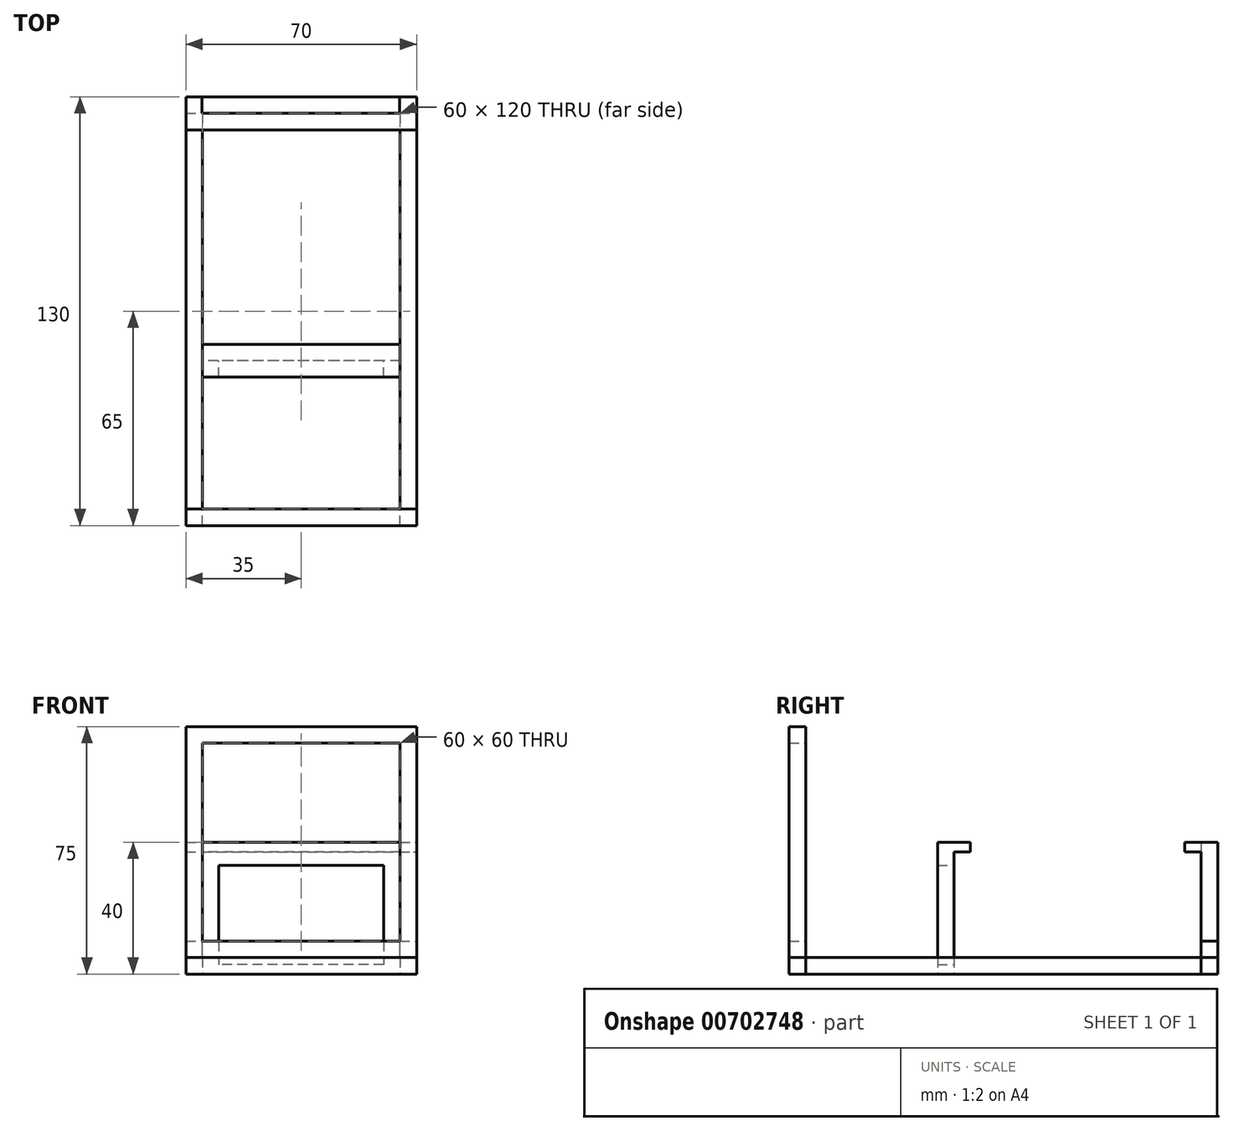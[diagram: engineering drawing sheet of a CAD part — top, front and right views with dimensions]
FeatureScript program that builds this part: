
annotation { "Feature Type Name" : "Feature", "Feature Type Description" : "" }
export const myFeature = defineFeature(function(context is Context, id is Id, definition is map)
    precondition{}
    {
        {
            var Q0;
            Q0=qCreatedBy(makeId("Top.planeOp"),FACE);
            var sketch = newSketch(context, id + "F0", { "sketchPlane" : qUnion([Q0])});
            skLineSegment(sketch, "E0.bottom", {"start": v(-35, 65) * mm, "end": v(35, 65) * mm});
            skLineSegment(sketch, "E0.top", {"start": v(-35, -65) * mm, "end": v(35, -65) * mm});
            skLineSegment(sketch, "E0.left", {"start": v(-35, 65) * mm, "end": v(-35, -65) * mm});
            skLineSegment(sketch, "E0.right", {"start": v(35, 65) * mm, "end": v(35, -65) * mm});
            skPoint(sketch, "E0.middle", {"position": v(0, 0) * mm});
            skLineSegment(sketch, "E1.bottom", {"start": v(-30, 60) * mm, "end": v(30, 60) * mm});
            skLineSegment(sketch, "E1.top", {"start": v(-30, -60) * mm, "end": v(30, -60) * mm});
            skLineSegment(sketch, "E1.left", {"start": v(-30, 60) * mm, "end": v(-30, -60) * mm});
            skLineSegment(sketch, "E1.right", {"start": v(30, 60) * mm, "end": v(30, -60) * mm});
            skLineSegment(sketch, "E2.bottom", {"start": v(-30, 60) * mm, "end": v(30, 60) * mm, "construction": true});
            skLineSegment(sketch, "E2.top", {"start": v(-30, -15) * mm, "end": v(30, -15) * mm, "construction": true});
            skLineSegment(sketch, "E2.left", {"start": v(-30, 60) * mm, "end": v(-30, -15) * mm, "construction": true});
            skLineSegment(sketch, "E2.right", {"start": v(30, 60) * mm, "end": v(30, -15) * mm, "construction": true});
            skLineSegment(sketch, "E3.bottom", {"start": v(-30, -15) * mm, "end": v(30, -15) * mm});
            skLineSegment(sketch, "E3.top", {"start": v(-30, -20) * mm, "end": v(30, -20) * mm});
            skLineSegment(sketch, "E3.left", {"start": v(-30, -15) * mm, "end": v(-30, -20) * mm});
            skLineSegment(sketch, "E3.right", {"start": v(30, -15) * mm, "end": v(30, -20) * mm});
            skLineSegment(sketch, "E4.top", {"start": v(-35, -60) * mm, "end": v(35, -60) * mm});
            skLineSegment(sketch, "E4.left", {"start": v(-35, -65) * mm, "end": v(-35, -60) * mm});
            skLineSegment(sketch, "E4.right", {"start": v(35, -65) * mm, "end": v(35, -60) * mm});
            skPoint(sketch, "E5.oppositeSnap0", {"position": v(0, 60) * mm});
            skLineSegment(sketch, "E5.top", {"start": v(-35, 60) * mm, "end": v(35, 60) * mm});
            skLineSegment(sketch, "E5.left", {"start": v(-35, 65) * mm, "end": v(-35, 60) * mm});
            skLineSegment(sketch, "E5.right", {"start": v(35, 65) * mm, "end": v(35, 60) * mm});
            skSolve(sketch);
        }
        {
            var Q0;
            Q0=makeQuery(id+"F0.imprint","IMPRINT",FACE,{"disambiguationData":[TD([[makeQuery(id+"F0.imprint","IMPRINT",EDGE,{"derivedFrom":sQuery(id+"F0.wireOp",EDGE,"E0.bottom")}),-1.0]])]});
            var Q1;
            Q1=makeQuery(id+"F0.imprint","IMPRINT",FACE,{"disambiguationData":[TD([[makeQuery(id+"F0.imprint","IMPRINT",EDGE,{"derivedFrom":sQuery(id+"F0.wireOp",EDGE,"E3.bottom")}),-1.0]])]});
            extrude(context, id + "F1", {"entities" : qUnion([Q0, Q1]), "depth" : 10 * mm, "offsetDistance" : 25 * mm});
        }
        {
            var Q0;
            Q0=makeQuery(id+"F0.imprint","IMPRINT",FACE,{"disambiguationData":[TD([[makeQuery(id+"F0.imprint","IMPRINT",EDGE,{"derivedFrom":sQuery(id+"F0.wireOp",EDGE,"E0.top")}),1.0]])]});
            extrude(context, id + "F2", {"entities" : qUnion([Q0]), "operationType" : NewBodyOperationType.ADD, "depth" : 75 * mm, "offsetDistance" : 25 * mm});
        }
        {
            var Q0;
            Q0=makeQuery(id+"F2.opExtrude","SWEPT_FACE",FACE,{"disambiguationData":[OSD([sQuery(id+"F0.wireOp",EDGE,"E4.top")])]});
            var sketch = newSketch(context, id + "F3", { "sketchPlane" : qUnion([Q0])});
            skLineSegment(sketch, "E6.bottom", {"start": v(-30, 10) * mm, "end": v(30, 10) * mm});
            skLineSegment(sketch, "E6.top", {"start": v(-30, 70) * mm, "end": v(30, 70) * mm});
            skLineSegment(sketch, "E6.left", {"start": v(-30, 10) * mm, "end": v(-30, 70) * mm});
            skLineSegment(sketch, "E6.right", {"start": v(30, 10) * mm, "end": v(30, 70) * mm});
            skSolve(sketch);
        }
        {
            var Q0;
            Q0=makeQuery(id+"F0.imprint","IMPRINT",FACE,{"disambiguationData":[TD([[makeQuery(id+"F0.imprint","IMPRINT",EDGE,{"derivedFrom":sQuery(id+"F0.wireOp",EDGE,"E3.bottom")}),-1.0]])]});
            extrude(context, id + "F4", {"entities" : qUnion([Q0]), "operationType" : NewBodyOperationType.ADD, "depth" : 40 * mm, "offsetDistance" : 25 * mm});
        }
        {
            var Q0;
            Q0=makeQuery(id+"F0.imprint","IMPRINT",FACE,{"disambiguationData":[TD([[makeQuery(id+"F0.imprint","IMPRINT",EDGE,{"derivedFrom":sQuery(id+"F0.wireOp",EDGE,"E0.bottom")}),-1.0]])]});
            extrude(context, id + "F5", {"entities" : qUnion([Q0]), "depth" : 40 * mm, "offsetDistance" : 25 * mm});
        }
        {
            var Q0;
            {var subQ6=sQuery(id+"F0.wireOp",EDGE,"E0.left");Q0=makeQuery(id+"F0.imprint","IMPRINT",FACE,{"disambiguationData":[TD([[makeQuery(id+"F0.imprint","IMPRINT",EDGE,{"derivedFrom":subQ6}),1.0]])]});}
            var Q1;
            {var subQ6=sQuery(id+"F0.wireOp",EDGE,"E0.right");Q1=makeQuery(id+"F0.imprint","IMPRINT",FACE,{"disambiguationData":[TD([[makeQuery(id+"F0.imprint","IMPRINT",EDGE,{"derivedFrom":subQ6}),-1.0]])]});}
            extrude(context, id + "F6", {"entities" : qUnion([Q0, Q1]), "depth" : 5 * mm, "offsetDistance" : 25 * mm});
        }
        {
            var Q0;
            {var subQ0=sQuery(id+"F0.wireOp",EDGE,"E3.bottom");Q0=makeQuery(id+"F4.boolean.opBoolean","MERGE",FACE,{"derivedFrom":[makeQuery(id+"F1.opExtrude","SWEPT_FACE",FACE,{"disambiguationData":[OSD([subQ0])]}),makeQuery(id+"F4.opExtrude","SWEPT_FACE",FACE,{"disambiguationData":[OSD([subQ0])]})]});}
            var sketch = newSketch(context, id + "F7", { "sketchPlane" : qUnion([Q0])});
            skLineSegment(sketch, "E7.bottom", {"start": v(-30, 40) * mm, "end": v(30, 40) * mm});
            skLineSegment(sketch, "E7.top", {"start": v(-30, 37) * mm, "end": v(30, 37) * mm});
            skLineSegment(sketch, "E7.left", {"start": v(-30, 40) * mm, "end": v(-30, 37) * mm});
            skLineSegment(sketch, "E7.right", {"start": v(30, 40) * mm, "end": v(30, 37) * mm});
            skLineSegment(sketch, "E8.bottom", {"start": v(-25, 32.92) * mm, "end": v(25, 32.92) * mm});
            skLineSegment(sketch, "E8.top", {"start": v(-25, 2.92) * mm, "end": v(25, 2.92) * mm});
            skLineSegment(sketch, "E8.left", {"start": v(-25, 32.92) * mm, "end": v(-25, 2.92) * mm});
            skLineSegment(sketch, "E8.right", {"start": v(25, 32.92) * mm, "end": v(25, 2.92) * mm});
            skPoint(sketch, "E8.middle", {"position": v(0, 17.92) * mm});
            skSolve(sketch);
        }
        {
            var Q0;
            Q0=makeQuery(id+"F5.opExtrude","SWEPT_FACE",FACE,{"disambiguationData":[OSD([sQuery(id+"F0.wireOp",EDGE,"E5.top")])]});
            var sketch = newSketch(context, id + "F8", { "sketchPlane" : qUnion([Q0])});
            skLineSegment(sketch, "E9.bottom", {"start": v(-35, 40) * mm, "end": v(35, 40) * mm});
            skLineSegment(sketch, "E9.top", {"start": v(-35, 37) * mm, "end": v(35, 37) * mm});
            skLineSegment(sketch, "E9.left", {"start": v(-35, 40) * mm, "end": v(-35, 37) * mm});
            skLineSegment(sketch, "E9.right", {"start": v(35, 40) * mm, "end": v(35, 37) * mm});
            skSolve(sketch);
        }
        {
            var Q0;
            Q0 = qSketchRegion(id + "F8", true);
            extrude(context, id + "F9", {"entities" : qUnion([Q0]), "operationType" : NewBodyOperationType.ADD, "depth" : 5 * mm, "offsetDistance" : 25 * mm});
        }
        {
            var Q0;
            Q0 = qSketchRegion(id + "F3", true);
            extrude(context, id + "F10", {"entities" : qUnion([Q0]), "operationType" : NewBodyOperationType.REMOVE, "oppositeDirection" : true, "depth" : 25 * mm, "offsetDistance" : 25 * mm});
        }
        {
            var Q0;
            Q0=makeQuery(id+"F7.imprint","IMPRINT",FACE,{"disambiguationData":[TD([[makeQuery(id+"F7.imprint","IMPRINT",EDGE,{"derivedFrom":sQuery(id+"F7.wireOp",EDGE,"E7.bottom")}),1.0]])]});
            extrude(context, id + "F11", {"entities" : qUnion([Q0]), "operationType" : NewBodyOperationType.ADD, "depth" : 5 * mm, "offsetDistance" : 25 * mm});
        }
        {
            var Q0;
            Q0=makeQuery(id+"F7.imprint","IMPRINT",FACE,{"disambiguationData":[TD([[makeQuery(id+"F7.imprint","IMPRINT",EDGE,{"derivedFrom":sQuery(id+"F7.wireOp",EDGE,"E8.bottom")}),-1.0]])]});
            extrude(context, id + "F12", {"entities" : qUnion([Q0]), "operationType" : NewBodyOperationType.REMOVE, "oppositeDirection" : true, "depth" : 5 * mm, "offsetDistance" : 25 * mm});
        }
        {
            var Q0;
            Q0=makeQuery(id+"F5.opExtrude","SWEPT_FACE",FACE,{"disambiguationData":[OSD([sQuery(id+"F0.wireOp",EDGE,"E0.bottom")])]});
            var sketch = newSketch(context, id + "F13", { "sketchPlane" : qUnion([Q0])});
            skLineSegment(sketch, "E10.bottom", {"start": v(-29.89, 40) * mm, "end": v(30.11, 40) * mm});
            skLineSegment(sketch, "E10.top", {"start": v(-29.89, 5) * mm, "end": v(30.11, 5) * mm});
            skLineSegment(sketch, "E10.left", {"start": v(-29.89, 40) * mm, "end": v(-29.89, 5) * mm});
            skLineSegment(sketch, "E10.right", {"start": v(30.11, 40) * mm, "end": v(30.11, 5) * mm});
            skSolve(sketch);
        }
        {
            var Q0;
            Q0=makeQuery(id+"F13.imprint","IMPRINT",FACE,{"disambiguationData":[TD([[makeQuery(id+"F13.imprint","IMPRINT",EDGE,{"derivedFrom":sQuery(id+"F13.wireOp",EDGE,"E10.bottom")}),1.0]])]});
            extrude(context, id + "F14", {"entities" : qUnion([Q0]), "operationType" : NewBodyOperationType.REMOVE, "oppositeDirection" : true, "depth" : 5 * mm, "offsetDistance" : 25 * mm});
        }
    });
